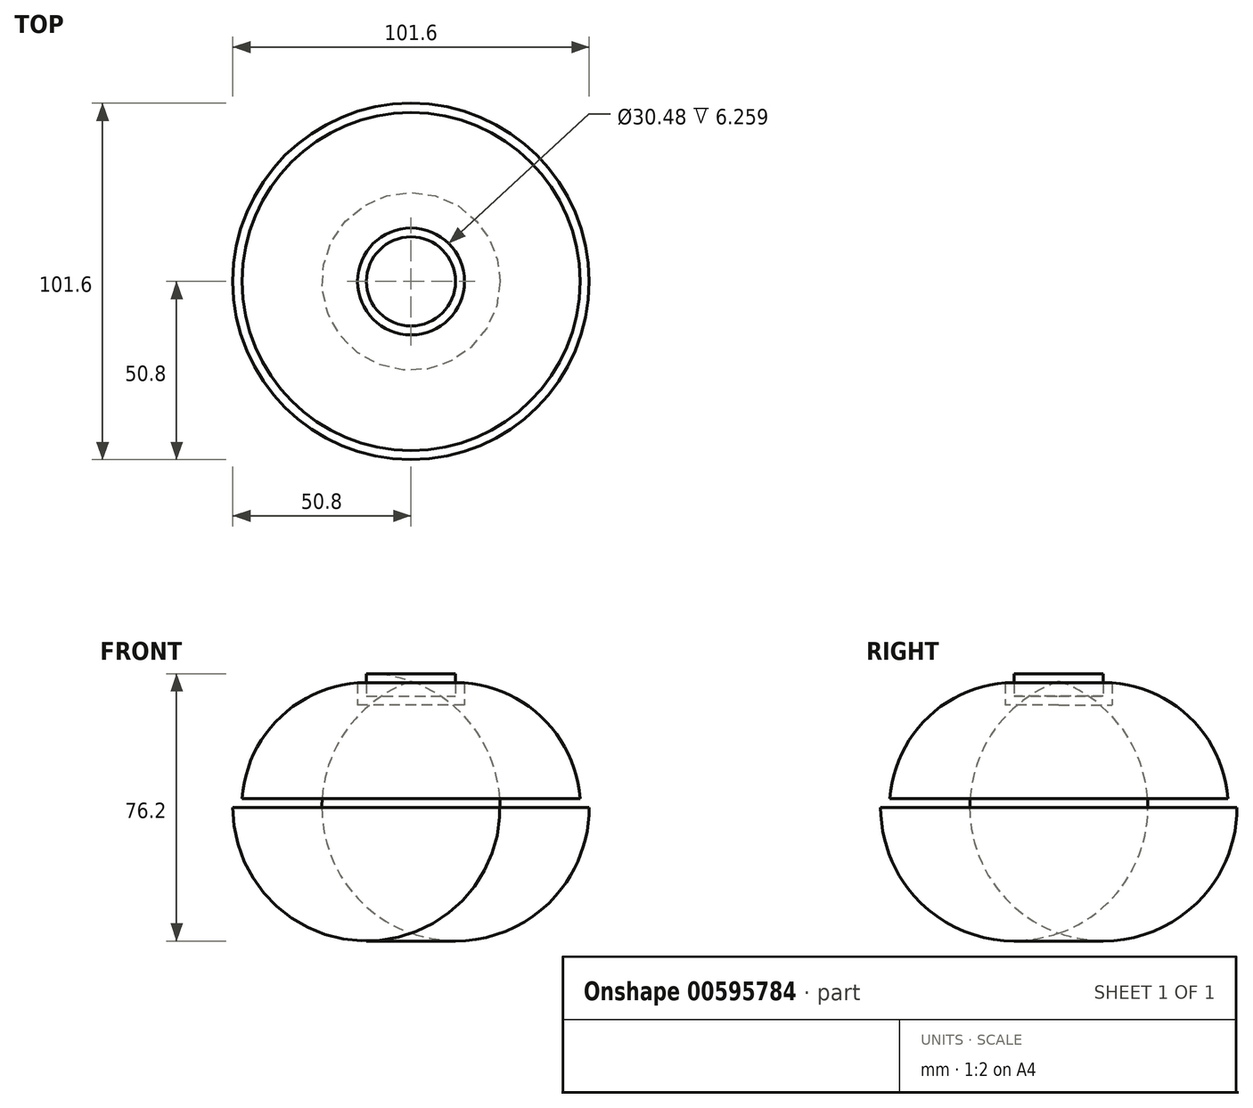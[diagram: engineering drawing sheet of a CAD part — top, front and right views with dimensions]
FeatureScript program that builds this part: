
annotation { "Feature Type Name" : "Feature", "Feature Type Description" : "" }
export const myFeature = defineFeature(function(context is Context, id is Id, definition is map)
    precondition{}
    {
        {
            var Q0;
            Q0=qCreatedBy(makeId("Right.planeOp"),FACE);
            var sketch = newSketch(context, id + "F0", { "sketchPlane" : qUnion([Q0])});
            skLineSegment(sketch, "E0", {"start": v(0, 0) * mm, "end": v(50.8, 0) * mm});
            skLineSegment(sketch, "E1", {"start": v(0, 0) * mm, "end": v(0, 38.1) * mm});
            skArc(sketch, "E2", {"start": v(12.7, 38.1) * mm, "mid": v(39.64, 26.94) * mm, "end": v(50.8, 0) * mm});
            skLineSegment(sketch, "E3", {"start": v(12.7, 38.1) * mm, "end": v(12.7, 31.75) * mm});
            skLineSegment(sketch, "E4", {"start": v(12.7, 31.75) * mm, "end": v(0, 31.75) * mm});
            skSolve(sketch);
        }
        {
            var Q0;
            Q0=makeQuery(id+"F0.imprint","IMPRINT",FACE,{"disambiguationData":[TD([[makeQuery(id+"F0.imprint","IMPRINT",EDGE,{"derivedFrom":sQuery(id+"F0.wireOp",EDGE,"E0")}),1.0]])]});
            var Q1;
            Q1=sQuery(id+"F0.wireOp",EDGE,"E1");
            revolve(context, id + "F1", {"entities" : qUnion([Q0]), "axis" : qUnion([Q1]), "revolveType" : RevolveType.FULL});
        }
        {
            var Q0;
            Q0=makeQuery(id+"F1.opRevolve","SWEPT_FACE",FACE,{"disambiguationData":[OSD([sQuery(id+"F0.wireOp",EDGE,"E2")])]});
            var Q1;
            Q1=makeQuery(id+"F1.opRevolve","SWEPT_BODY",BODY,{"disambiguationData":[OSD([sQuery(id+"F0.wireOp",EDGE,"E0"),sQuery(id+"F0.wireOp",EDGE,"E1"),sQuery(id+"F0.wireOp",EDGE,"E2"),sQuery(id+"F0.wireOp",EDGE,"E3"),sQuery(id+"F0.wireOp",EDGE,"E4")])]});
            shell(context, id + "F2", {"isHollow" : true, "entities" : qUnion([Q0]), "parts" : qUnion([Q1]), "thickness" : 2.54 * mm});
        }
    });
